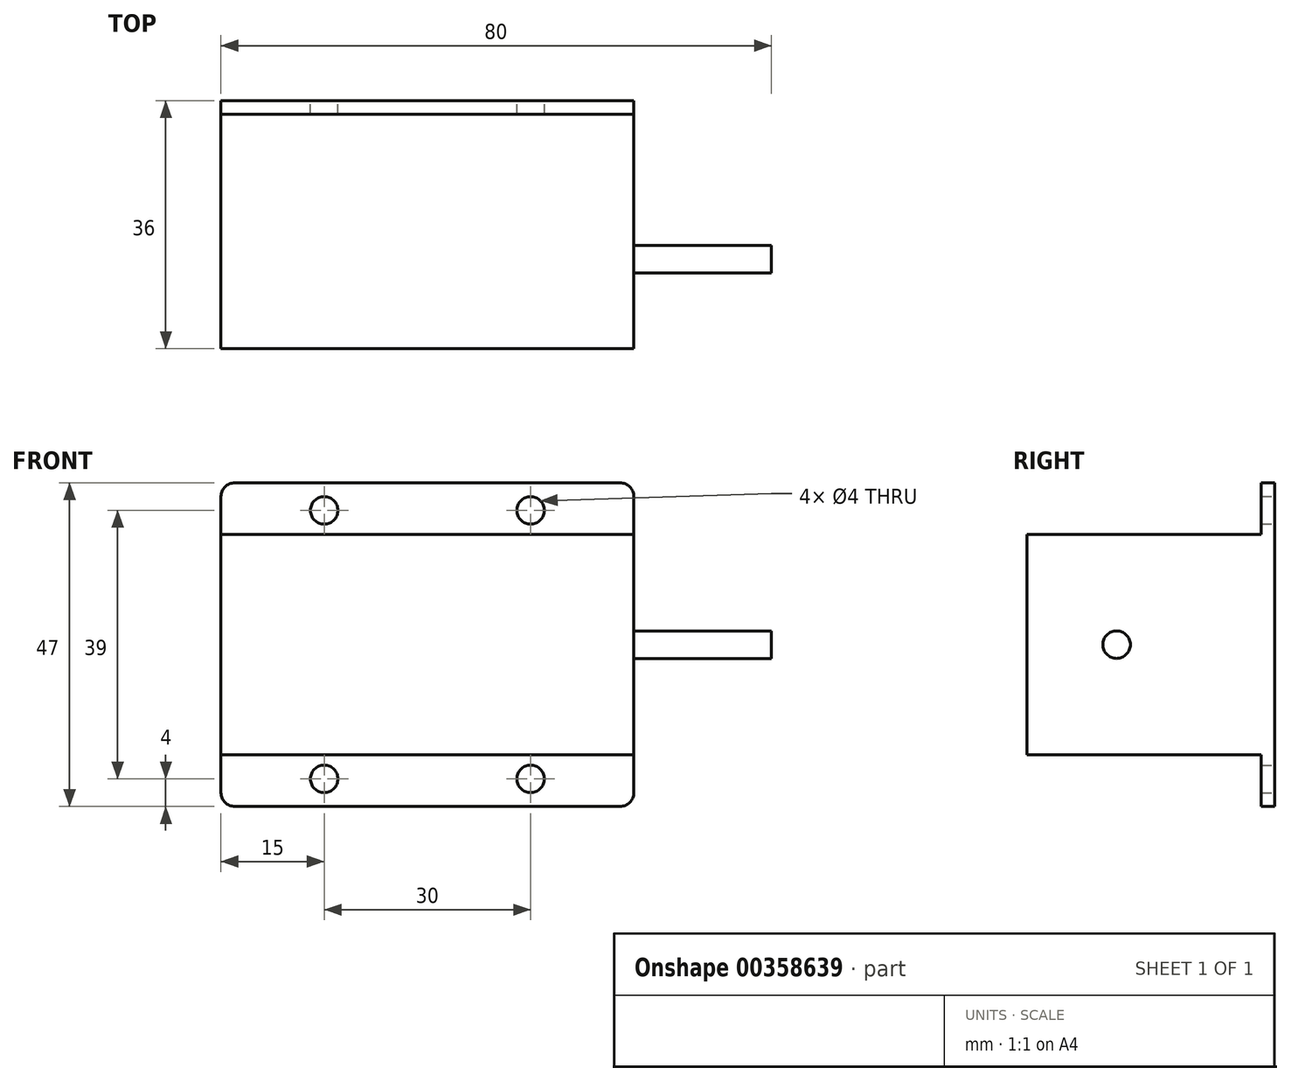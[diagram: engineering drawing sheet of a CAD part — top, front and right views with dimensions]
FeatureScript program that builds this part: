
annotation { "Feature Type Name" : "Feature", "Feature Type Description" : "" }
export const myFeature = defineFeature(function(context is Context, id is Id, definition is map)
    precondition{}
    {
        {
            var Q0;
            Q0=qCreatedBy(makeId("Front.planeOp"),FACE);
            var sketch = newSketch(context, id + "F0", { "sketchPlane" : qUnion([Q0])});
            skLineSegment(sketch, "E0.bottom", {"start": v(28, 23.5) * mm, "end": v(-28, 23.5) * mm});
            skLineSegment(sketch, "E0.top", {"start": v(28, -23.5) * mm, "end": v(-28, -23.5) * mm});
            skLineSegment(sketch, "E0.left", {"start": v(30, 21.5) * mm, "end": v(30, -21.5) * mm});
            skLineSegment(sketch, "E0.right", {"start": v(-30, 21.5) * mm, "end": v(-30, -21.5) * mm});
            skPoint(sketch, "E0.middle", {"position": v(0, 0) * mm});
            skPoint(sketch, "E1.visualSharp", {"position": v(-30, 23.5) * mm});
            skArc(sketch, "E1.filletArc", {"start": v(-28, 23.5) * mm, "mid": v(-29.41, 22.91) * mm, "end": v(-30, 21.5) * mm});
            skPoint(sketch, "E2.visualSharp", {"position": v(30, 23.5) * mm});
            skArc(sketch, "E2.filletArc", {"start": v(30, 21.5) * mm, "mid": v(29.41, 22.91) * mm, "end": v(28, 23.5) * mm});
            skPoint(sketch, "E3.visualSharp", {"position": v(30, -23.5) * mm});
            skArc(sketch, "E3.filletArc", {"start": v(28, -23.5) * mm, "mid": v(29.41, -22.91) * mm, "end": v(30, -21.5) * mm});
            skPoint(sketch, "E4.visualSharp", {"position": v(-30, -23.5) * mm});
            skLineSegment(sketch, "E5.bottom", {"start": v(15, 19.5) * mm, "end": v(-15, 19.5) * mm, "construction": true});
            skLineSegment(sketch, "E5.top", {"start": v(15, -19.5) * mm, "end": v(-15, -19.5) * mm, "construction": true});
            skLineSegment(sketch, "E5.left", {"start": v(15, 19.5) * mm, "end": v(15, -19.5) * mm, "construction": true});
            skLineSegment(sketch, "E5.right", {"start": v(-15, 19.5) * mm, "end": v(-15, -19.5) * mm, "construction": true});
            skCircle(sketch, "E6", {"center": v(-15, 19.5) * mm, "radius": 2 * mm});
            skCircle(sketch, "E7", {"center": v(15, 19.5) * mm, "radius": 2 * mm});
            skCircle(sketch, "E8", {"center": v(15, -19.5) * mm, "radius": 2 * mm});
            skCircle(sketch, "E9", {"center": v(-15, -19.5) * mm, "radius": 2 * mm});
            skArc(sketch, "E10.filletArc", {"start": v(-30, -21.5) * mm, "mid": v(-29.41, -22.91) * mm, "end": v(-28, -23.5) * mm});
            skSolve(sketch);
        }
        {
            var Q0;
            Q0 = qSketchRegion(id + "F0", true);
            extrude(context, id + "F1", {"entities" : qUnion([Q0]), "depth" : 2 * mm, "offsetDistance" : 25 * mm});
        }
        {
            var Q0;
            Q0=qCreatedBy(makeId("Front.planeOp"),FACE);
            var sketch = newSketch(context, id + "F2", { "sketchPlane" : qUnion([Q0])});
            skLineSegment(sketch, "E11.bottom", {"start": v(30, 16) * mm, "end": v(-30, 16) * mm});
            skLineSegment(sketch, "E11.top", {"start": v(30, -16) * mm, "end": v(-30, -16) * mm});
            skLineSegment(sketch, "E11.left", {"start": v(30, 16) * mm, "end": v(30, -16) * mm});
            skLineSegment(sketch, "E11.right", {"start": v(-30, 16) * mm, "end": v(-30, -16) * mm});
            skPoint(sketch, "E11.middle", {"position": v(0, 0) * mm});
            skSolve(sketch);
        }
        {
            var Q0;
            Q0 = qSketchRegion(id + "F2", true);
            extrude(context, id + "F3", {"entities" : qUnion([Q0]), "operationType" : NewBodyOperationType.ADD, "depth" : (36) * mm, "offsetDistance" : 25 * mm});
        }
        {
            var Q0;
            Q0=makeQuery(id+"F3.boolean.opBoolean","MERGE",FACE,{"derivedFrom":[makeQuery(id+"F1.opExtrude","SWEPT_FACE",FACE,{"disambiguationData":[OSD([sQuery(id+"F0.wireOp",EDGE,"E0.left")])]}),makeQuery(id+"F3.opExtrude","SWEPT_FACE",FACE,{"disambiguationData":[OSD([sQuery(id+"F2.wireOp",EDGE,"E11.left")])]})]});
            var sketch = newSketch(context, id + "F4", { "sketchPlane" : qUnion([Q0])});
            skCircle(sketch, "E12", {"center": v(-23, 0) * mm, "radius": 2 * mm});
            skSolve(sketch);
        }
        {
            var Q0;
            Q0 = qSketchRegion(id + "F4", true);
            extrude(context, id + "F5", {"entities" : qUnion([Q0]), "operationType" : NewBodyOperationType.ADD, "depth" : 20 * mm, "offsetDistance" : 25 * mm});
        }
    });
